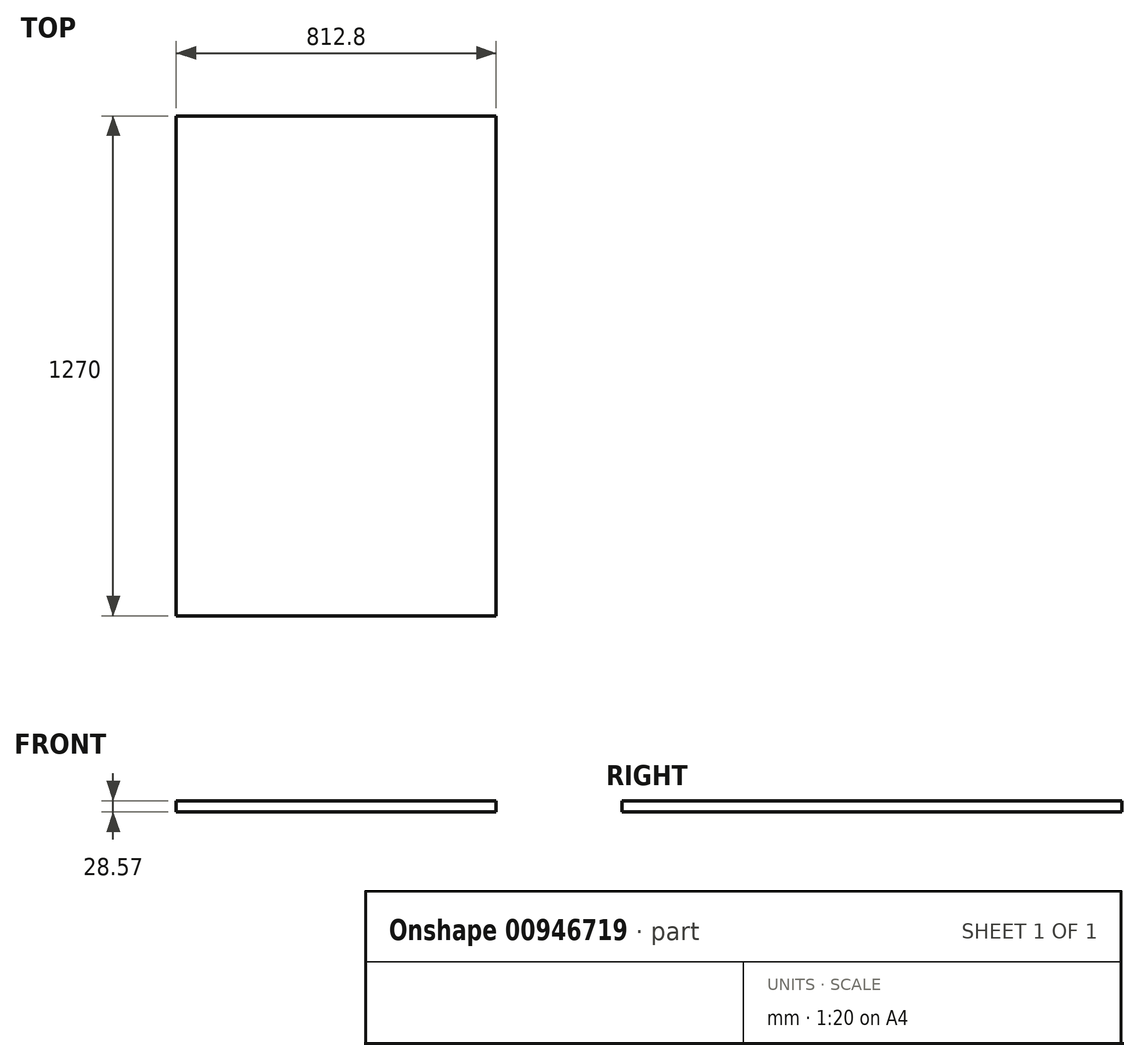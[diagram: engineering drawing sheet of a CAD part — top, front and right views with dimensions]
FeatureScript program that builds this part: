
annotation { "Feature Type Name" : "Feature", "Feature Type Description" : "" }
export const myFeature = defineFeature(function(context is Context, id is Id, definition is map)
    precondition{}
    {
        {
            var Q0;
            Q0=qCreatedBy(makeId("Top.planeOp"),FACE);
            var sketch = newSketch(context, id + "F0", { "sketchPlane" : qUnion([Q0])});
            skLineSegment(sketch, "E0.bottom", {"start": v(406.4, 635) * mm, "end": v(-406.4, 635) * mm});
            skLineSegment(sketch, "E0.top", {"start": v(406.4, -635) * mm, "end": v(-406.4, -635) * mm});
            skLineSegment(sketch, "E0.left", {"start": v(406.4, 635) * mm, "end": v(406.4, -635) * mm});
            skLineSegment(sketch, "E0.right", {"start": v(-406.4, 635) * mm, "end": v(-406.4, -635) * mm});
            skPoint(sketch, "E0.middle", {"position": v(0, 0) * mm});
            skSolve(sketch);
        }
        {
            var Q0;
            Q0=makeQuery(id+"F0.imprint","IMPRINT",FACE,{"disambiguationData":[TD([[makeQuery(id+"F0.imprint","IMPRINT",EDGE,{"derivedFrom":sQuery(id+"F0.wireOp",EDGE,"E0.bottom")}),1.0]])]});
            extrude(context, id + "F1", {"entities" : qUnion([Q0]), "depth" : 28.57 * mm, "offsetDistance" : 25.4 * mm});
        }
    });
